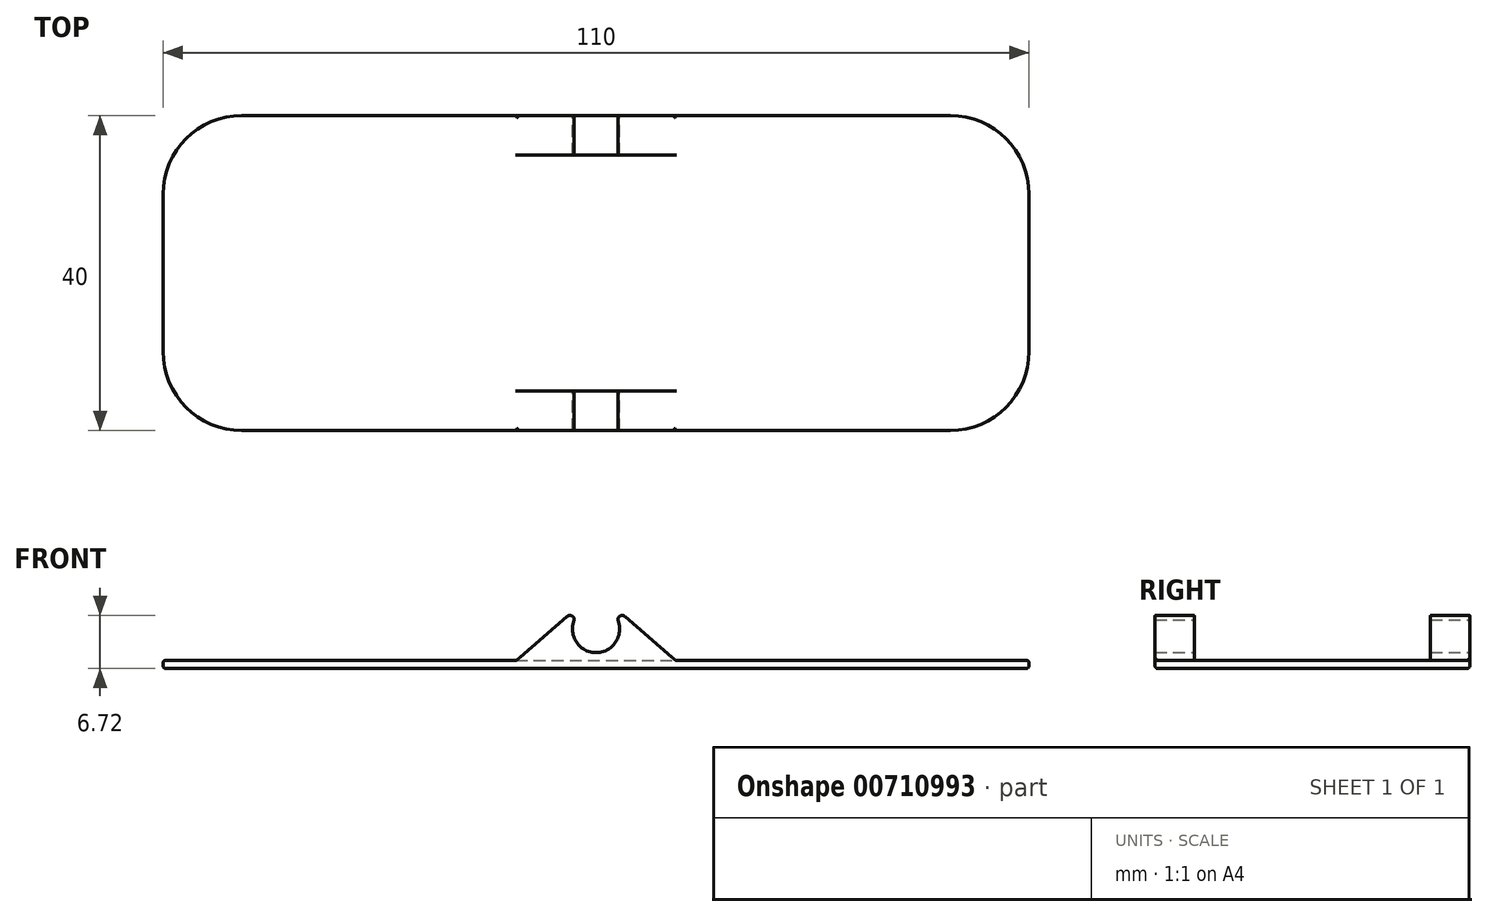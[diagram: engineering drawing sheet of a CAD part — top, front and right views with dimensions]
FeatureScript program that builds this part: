
annotation { "Feature Type Name" : "Feature", "Feature Type Description" : "" }
export const myFeature = defineFeature(function(context is Context, id is Id, definition is map)
    precondition{}
    {
        {
            var Q0;
            Q0=qCreatedBy(makeId("Top.planeOp"),FACE);
            var sketch = newSketch(context, id + "F0", { "sketchPlane" : qUnion([Q0])});
            skLineSegment(sketch, "E0.bottom", {"start": v(-45, 20) * mm, "end": v(45, 20) * mm});
            skLineSegment(sketch, "E0.top", {"start": v(-45, -20) * mm, "end": v(45, -20) * mm});
            skLineSegment(sketch, "E0.left", {"start": v(-55, 10) * mm, "end": v(-55, -10) * mm});
            skLineSegment(sketch, "E0.right", {"start": v(55, 10) * mm, "end": v(55, -10) * mm});
            skPoint(sketch, "E1.visualSharp", {"position": v(-55, 20) * mm});
            skArc(sketch, "E1.filletArc", {"start": v(-45, 20) * mm, "mid": v(-52.07, 17.07) * mm, "end": v(-55, 10) * mm});
            skPoint(sketch, "E2.visualSharp", {"position": v(55, 20) * mm});
            skArc(sketch, "E2.filletArc", {"start": v(55, 10) * mm, "mid": v(52.07, 17.07) * mm, "end": v(45, 20) * mm});
            skPoint(sketch, "E3.visualSharp", {"position": v(55, -20) * mm});
            skArc(sketch, "E3.filletArc", {"start": v(45, -20) * mm, "mid": v(52.07, -17.07) * mm, "end": v(55, -10) * mm});
            skPoint(sketch, "E4.visualSharp", {"position": v(-55, -20) * mm});
            skArc(sketch, "E4.filletArc", {"start": v(-55, -10) * mm, "mid": v(-52.07, -17.07) * mm, "end": v(-45, -20) * mm});
            skArc(sketch, "E5.0", {"start": v(-54.2, -10) * mm, "mid": v(-51.5, -16.5) * mm, "end": v(-45, -19.2) * mm});
            skLineSegment(sketch, "E5.1", {"start": v(-54.2, 10) * mm, "end": v(-54.2, -10) * mm});
            skLineSegment(sketch, "E5.2", {"start": v(-45, -19.2) * mm, "end": v(45, -19.2) * mm});
            skArc(sketch, "E5.3", {"start": v(-45, 19.2) * mm, "mid": v(-51.5, 16.5) * mm, "end": v(-54.2, 10) * mm});
            skArc(sketch, "E5.4", {"start": v(45, -19.2) * mm, "mid": v(51.5, -16.5) * mm, "end": v(54.2, -10) * mm});
            skLineSegment(sketch, "E5.5", {"start": v(54.2, 10) * mm, "end": v(54.2, -10) * mm});
            skArc(sketch, "E5.6", {"start": v(54.2, 10) * mm, "mid": v(51.5, 16.5) * mm, "end": v(45, 19.2) * mm});
            skLineSegment(sketch, "E5.7", {"start": v(-45, 19.2) * mm, "end": v(45, 19.2) * mm});
            skSolve(sketch);
        }
        {
            var Q0;
            Q0 = qSketchRegion(id + "F0", true);
            var Q1;
            Q1=makeQuery(id+"F0.imprint","IMPRINT",FACE,{"disambiguationData":[TD([[makeQuery(id+"F0.imprint","IMPRINT",EDGE,{"derivedFrom":sQuery(id+"F0.wireOp",EDGE,"E5.0")}),1.0]])]});
            extrude(context, id + "F1", {"entities" : qUnion([Q0, Q1]), "depth" : 2 * mm, "offsetDistance" : 25 * mm});
        }
        {
            var Q0;
            Q0=makeQuery(id+"F1.opExtrude","SWEPT_FACE",FACE,{"disambiguationData":[OSD([sQuery(id+"F0.wireOp",EDGE,"E0.bottom")])]});
            var sketch = newSketch(context, id + "F2", { "sketchPlane" : qUnion([Q0])});
            skArc(sketch, "E6", {"start": v(-2.78, 7.13) * mm, "mid": v(0, 3) * mm, "end": v(2.78, 7.13) * mm});
            skArc(sketch, "E7", {"start": v(3.67, 7.58) * mm, "mid": v(3.08, 7.66) * mm, "end": v(2.78, 7.13) * mm});
            skArc(sketch, "E8.MirrorCS", {"start": v(-3.67, 7.58) * mm, "mid": v(-3.08, 7.66) * mm, "end": v(-2.78, 7.13) * mm});
            skLineSegment(sketch, "E9", {"start": v(-10.12, 2) * mm, "end": v(10.12, 2) * mm});
            skLineSegment(sketch, "E10", {"start": v(3.67, 7.58) * mm, "end": v(10.12, 2) * mm});
            skPoint(sketch, "E11.trimOffspring.start.orphan", {"position": v(4, 6) * mm});
            skLineSegment(sketch, "E12.MirrorCS", {"start": v(-3.67, 7.58) * mm, "end": v(-10.12, 2) * mm});
            skPoint(sketch, "E13.MirrorCS.start.orphan", {"position": v(-4, 6) * mm});
            skSolve(sketch);
        }
        {
            var Q0;
            Q0 = qSketchRegion(id + "F2", true);
            var Q1;
            Q1=makeQuery(id+"F1.opExtrude","SWEPT_FACE",FACE,{"disambiguationData":[OSD([sQuery(id+"F0.wireOp",EDGE,"E0.top")])]});
            extrude(context, id + "F3", {"entities" : qUnion([Q0]), "operationType" : NewBodyOperationType.ADD, "endBound" : BoundingType.UP_TO_SURFACE, "oppositeDirection" : true, "depth" : 25 * mm, "endBoundEntityFace" : qUnion([Q1]), "offsetDistance" : 25 * mm});
        }
        {
            var Q0;
            Q0=makeQuery(id+"F1.opExtrude","CAP_FACE",FACE,{"disambiguationData":[OSD([sQuery(id+"F0.wireOp",EDGE,"E0.bottom"),sQuery(id+"F0.wireOp",EDGE,"E0.top"),sQuery(id+"F0.wireOp",EDGE,"E0.left"),sQuery(id+"F0.wireOp",EDGE,"E0.right"),sQuery(id+"F0.wireOp",EDGE,"E1.filletArc"),sQuery(id+"F0.wireOp",EDGE,"E2.filletArc"),sQuery(id+"F0.wireOp",EDGE,"E3.filletArc"),sQuery(id+"F0.wireOp",EDGE,"E4.filletArc")])],"isStart":true});
            var Q1;
            {var subQ0=sQuery(id+"F0.wireOp",EDGE,"E2.filletArc");var subQ1=sQuery(id+"F0.wireOp",EDGE,"E0.top");var subQ3=sQuery(id+"F0.wireOp",EDGE,"E0.right");var subQ4=sQuery(id+"F0.wireOp",EDGE,"E0.bottom");var subQ5=sQuery(id+"F0.wireOp",EDGE,"E3.filletArc");Q1=makeQuery(id+"F3.boolean.opBoolean","SPLIT",FACE,{"disambiguationData":[TD([makeQuery(id+"F1.opExtrude","SWEPT_FACE",FACE,{"disambiguationData":[OSD([subQ3])]})])],"derivedFrom":makeQuery(id+"F1.opExtrude","CAP_FACE",FACE,{"disambiguationData":[OSD([subQ4,subQ1,sQuery(id+"F0.wireOp",EDGE,"E0.left"),subQ3,sQuery(id+"F0.wireOp",EDGE,"E1.filletArc"),subQ0,subQ5,sQuery(id+"F0.wireOp",EDGE,"E4.filletArc")])],"isStart":false})});}
            var Q2;
            {var subQ0=sQuery(id+"F0.wireOp",EDGE,"E1.filletArc");var subQ1=sQuery(id+"F0.wireOp",EDGE,"E0.left");var subQ2=sQuery(id+"F0.wireOp",EDGE,"E0.top");var subQ4=sQuery(id+"F0.wireOp",EDGE,"E0.bottom");var subQ5=sQuery(id+"F0.wireOp",EDGE,"E4.filletArc");Q2=makeQuery(id+"F3.boolean.opBoolean","SPLIT",FACE,{"disambiguationData":[TD([makeQuery(id+"F1.opExtrude","SWEPT_FACE",FACE,{"disambiguationData":[OSD([subQ1])]})])],"derivedFrom":makeQuery(id+"F1.opExtrude","CAP_FACE",FACE,{"disambiguationData":[OSD([subQ4,subQ2,subQ1,sQuery(id+"F0.wireOp",EDGE,"E0.right"),subQ0,sQuery(id+"F0.wireOp",EDGE,"E2.filletArc"),sQuery(id+"F0.wireOp",EDGE,"E3.filletArc"),subQ5])],"isStart":false})});}
            fillet(context, id + "F4", {"entities" : qUnion([Q0, Q1, Q2]), "radius" : .3 * mm, "tangentPropagation" : true, "allowEdgeOverflow" : false});
        }
        {
            var Q0;
            {var subQ0=sQuery(id+"F0.wireOp",EDGE,"E1.filletArc");var subQ1=sQuery(id+"F0.wireOp",EDGE,"E0.left");var subQ2=sQuery(id+"F0.wireOp",EDGE,"E0.top");var subQ4=sQuery(id+"F0.wireOp",EDGE,"E0.bottom");var subQ5=sQuery(id+"F0.wireOp",EDGE,"E4.filletArc");Q0=makeQuery(id+"F3.boolean.opBoolean","SPLIT",FACE,{"disambiguationData":[TD([makeQuery(id+"F1.opExtrude","SWEPT_FACE",FACE,{"disambiguationData":[OSD([subQ1])]})])],"derivedFrom":makeQuery(id+"F1.opExtrude","CAP_FACE",FACE,{"disambiguationData":[OSD([subQ4,subQ2,subQ1,sQuery(id+"F0.wireOp",EDGE,"E0.right"),subQ0,sQuery(id+"F0.wireOp",EDGE,"E2.filletArc"),sQuery(id+"F0.wireOp",EDGE,"E3.filletArc"),subQ5])],"isStart":false})});}
            var sketch = newSketch(context, id + "F5", { "sketchPlane" : qUnion([Q0])});
            skLineSegment(sketch, "E14.bottom", {"start": v(-21.66, 15) * mm, "end": v(22.64, 15) * mm});
            skLineSegment(sketch, "E14.top", {"start": v(-21.66, -15) * mm, "end": v(22.64, -15) * mm});
            skLineSegment(sketch, "E14.left", {"start": v(-21.66, 15) * mm, "end": v(-21.66, -15) * mm});
            skLineSegment(sketch, "E14.right", {"start": v(22.64, 15) * mm, "end": v(22.64, -15) * mm});
            skSolve(sketch);
        }
        {
            var Q0;
            Q0 = qSketchRegion(id + "F5", true);
            extrude(context, id + "F6", {"entities" : qUnion([Q0]), "operationType" : NewBodyOperationType.REMOVE, "depth" : 25 * mm, "offsetDistance" : 25 * mm});
        }
        {
            var Q0;
            {var subQ0=sQuery(id+"F0.wireOp",EDGE,"E0.top");Q0=makeQuery(id+"F3.boolean.opBoolean","MERGE",FACE,{"derivedFrom":[makeQuery(id+"F1.opExtrude","SWEPT_FACE",FACE,{"disambiguationData":[OSD([subQ0])]}),makeQuery(id+"F3.opExtrude","CAP_FACE",FACE,{"disambiguationData":[OSD([subQ0])],"isStart":false})]});}
            var sketch = newSketch(context, id + "F7", { "sketchPlane" : qUnion([Q0])});
            skLineSegment(sketch, "E15.bottom", {"start": v(-74.5, 1) * mm, "end": v(73.02, 1) * mm});
            skLineSegment(sketch, "E15.top", {"start": v(-74.5, -17.1) * mm, "end": v(73.02, -17.1) * mm});
            skLineSegment(sketch, "E15.left", {"start": v(-74.5, 1) * mm, "end": v(-74.5, -17.1) * mm});
            skLineSegment(sketch, "E15.right", {"start": v(73.02, 1) * mm, "end": v(73.02, -17.1) * mm});
            skSolve(sketch);
        }
        {
            var Q0;
            Q0 = qSketchRegion(id + "F7", true);
            extrude(context, id + "F8", {"entities" : qUnion([Q0]), "operationType" : NewBodyOperationType.REMOVE, "endBound" : BoundingType.THROUGH_ALL, "oppositeDirection" : true, "depth" : 25 * mm, "offsetDistance" : 25 * mm});
        }
        {
            var Q0;
            Q0=makeQuery(id+"F8.boolean.opBoolean","COPY",FACE,{"derivedFrom":makeQuery(id+"F8.opExtrude","SWEPT_FACE",FACE,{"disambiguationData":[OSD([sQuery(id+"F7.wireOp",EDGE,"E15.bottom")])]})});
            fillet(context, id + "F9", {"entities" : qUnion([Q0]), "radius" : .3 * mm, "tangentPropagation" : true, "allowEdgeOverflow" : false});
        }
    });
